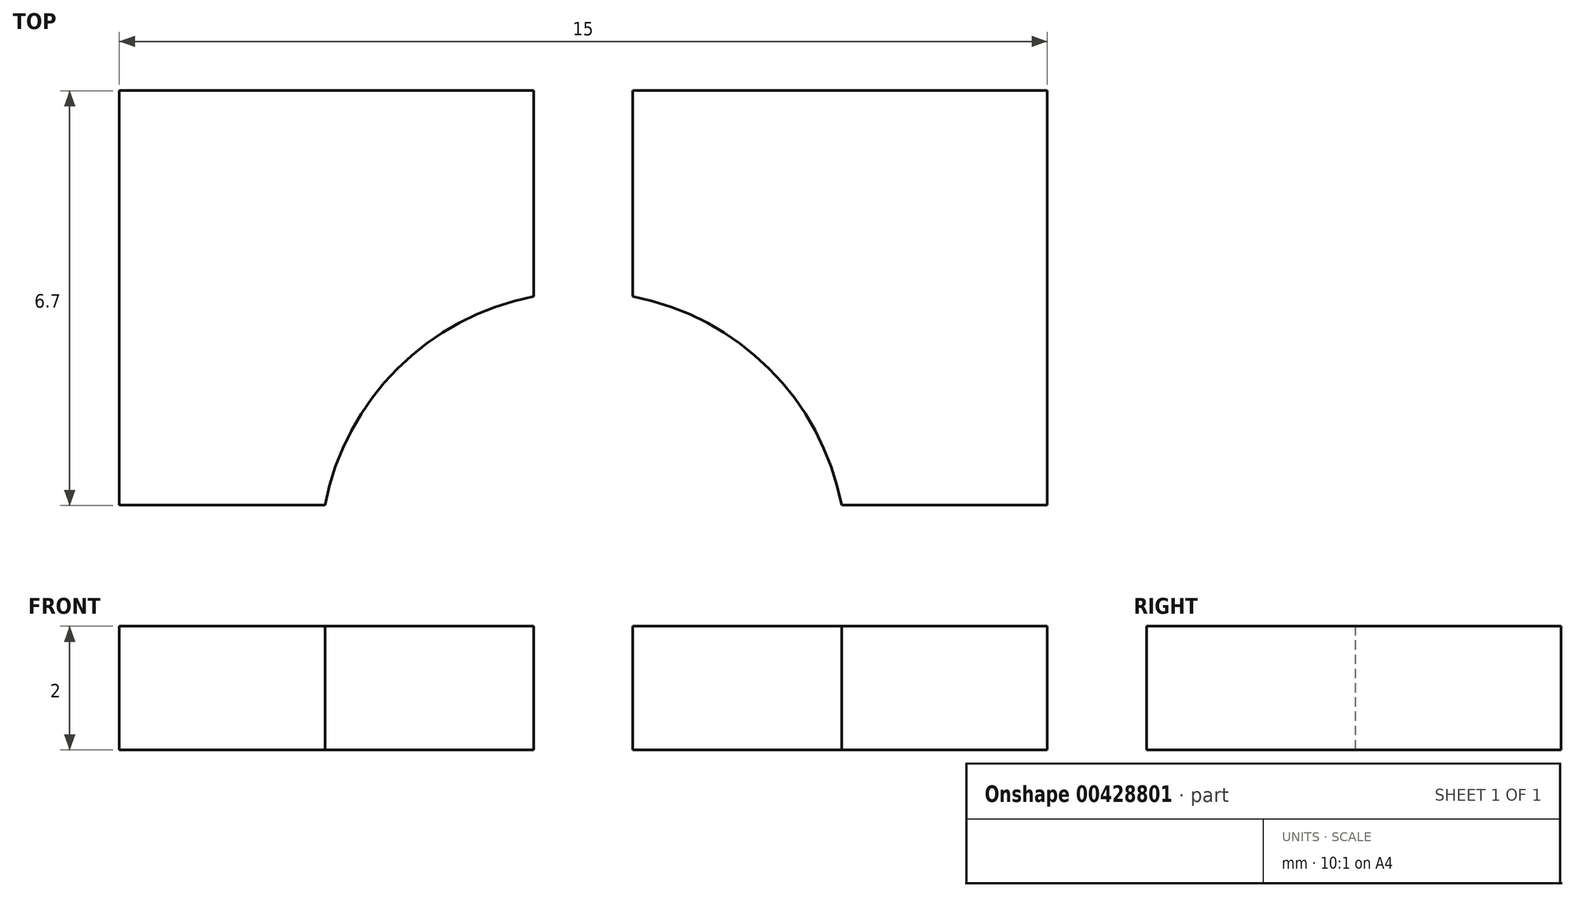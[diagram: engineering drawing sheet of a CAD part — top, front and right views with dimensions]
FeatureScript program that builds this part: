
annotation { "Feature Type Name" : "Feature", "Feature Type Description" : "" }
export const myFeature = defineFeature(function(context is Context, id is Id, definition is map)
    precondition{}
    {
        {
            var Q0;
            Q0=qCreatedBy(makeId("Top.planeOp"),FACE);
            var sketch = newSketch(context, id + "F0", { "sketchPlane" : qUnion([Q0])});
            skLineSegment(sketch, "E0.bottom", {"start": v(-8.3, -12.26) * mm, "end": v(6.7, -12.26) * mm});
            skLineSegment(sketch, "E0.top", {"start": v(-8.3, -27.26) * mm, "end": v(6.7, -27.26) * mm});
            skLineSegment(sketch, "E0.left", {"start": v(-8.3, -12.26) * mm, "end": v(-8.3, -27.26) * mm});
            skLineSegment(sketch, "E0.right", {"start": v(6.7, -12.26) * mm, "end": v(6.7, -27.26) * mm});
            skLineSegment(sketch, "E1.bottom", {"start": v(-8.3, -12.26) * mm, "end": v(-1.6, -12.26) * mm});
            skLineSegment(sketch, "E1.top", {"start": v(-8.3, -18.96) * mm, "end": v(-4.97, -18.96) * mm});
            skLineSegment(sketch, "E1.left", {"start": v(-8.3, -12.26) * mm, "end": v(-8.3, -18.96) * mm});
            skLineSegment(sketch, "E1.right", {"start": v(-1.6, -12.26) * mm, "end": v(-1.6, -15.58) * mm});
            skLineSegment(sketch, "E2.bottom", {"start": v(-8.3, -27.26) * mm, "end": v(-1.6, -27.26) * mm});
            skLineSegment(sketch, "E2.top", {"start": v(-8.3, -20.56) * mm, "end": v(-4.97, -20.56) * mm});
            skLineSegment(sketch, "E2.left", {"start": v(-8.3, -27.26) * mm, "end": v(-8.3, -20.56) * mm});
            skLineSegment(sketch, "E2.right", {"start": v(-1.6, -27.26) * mm, "end": v(-1.6, -23.93) * mm});
            skLineSegment(sketch, "E3.bottom", {"start": v(6.7, -27.26) * mm, "end": v(0, -27.26) * mm});
            skLineSegment(sketch, "E3.top", {"start": v(6.7, -20.56) * mm, "end": v(3.37, -20.56) * mm});
            skLineSegment(sketch, "E3.left", {"start": v(6.7, -27.26) * mm, "end": v(6.7, -20.56) * mm});
            skLineSegment(sketch, "E3.right", {"start": v(0, -27.26) * mm, "end": v(0, -23.93) * mm});
            skLineSegment(sketch, "E4.bottom", {"start": v(6.7, -12.26) * mm, "end": v(0, -12.26) * mm});
            skLineSegment(sketch, "E4.top", {"start": v(6.7, -18.96) * mm, "end": v(3.37, -18.96) * mm});
            skLineSegment(sketch, "E4.left", {"start": v(6.7, -12.26) * mm, "end": v(6.7, -18.96) * mm});
            skLineSegment(sketch, "E4.right", {"start": v(0, -12.26) * mm, "end": v(0, -15.58) * mm});
            skCircle(sketch, "E5", {"center": v(-0.8, -19.76) * mm, "radius": 3 * mm});
            skPoint(sketch, "E5.centerSnap0", {"position": v(6.7, -19.76) * mm});
            skPoint(sketch, "E5.centerSnap1", {"position": v(-0.8, -12.26) * mm});
            skArc(sketch, "E6", {"start": v(-4.97, -20.56) * mm, "mid": v(-3.8, -22.76) * mm, "end": v(-1.6, -23.93) * mm});
            skPoint(sketch, "E7.orphan", {"position": v(0, -18.96) * mm});
            skArc(sketch, "E8.trimOffspring", {"start": v(0, -23.93) * mm, "mid": v(2.2, -22.76) * mm, "end": v(3.37, -20.56) * mm});
            skArc(sketch, "E9.trimOffspring", {"start": v(3.37, -18.96) * mm, "mid": v(2.2, -16.75) * mm, "end": v(0, -15.58) * mm});
            skArc(sketch, "E10.trimOffspring", {"start": v(-1.6, -15.58) * mm, "mid": v(-3.8, -16.75) * mm, "end": v(-4.97, -18.96) * mm});
            skSolve(sketch);
        }
        {
            var Q0;
            Q0=makeQuery(id+"F0.imprint","IMPRINT",FACE,{"disambiguationData":[TD([[makeQuery(id+"F0.imprint","IMPRINT",EDGE,{"derivedFrom":sQuery(id+"F0.wireOp",EDGE,"E0.bottom")}),-1.0]])]});
            extrude(context, id + "F1", {"entities" : qUnion([Q0]), "depth" : 2 * mm});
        }
    });
